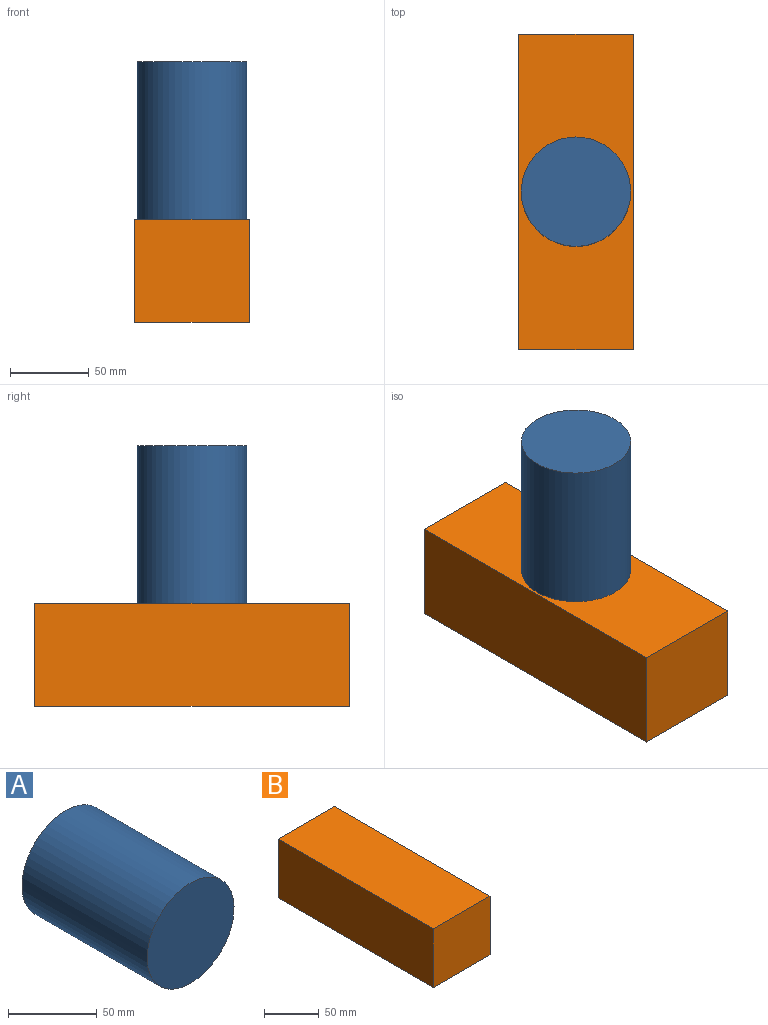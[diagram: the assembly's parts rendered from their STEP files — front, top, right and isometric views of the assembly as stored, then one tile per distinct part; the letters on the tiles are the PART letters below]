
ASSEMBLY  parts=2 mates=1
PART A: 3 faces, bbox 69.4x100x69.4 mm
  f0: cylinder r=34.71mm len=100mm, axis (0,1,0), area 21808.6mm2, adj f1,f2
  f1: plane 69.42x69.42mm, normal (0,-1,0), area 3784.8mm2, adj f0
  f2: plane 69.42x69.42mm, normal (0,1,0), area 3784.8mm2, adj f0
PART B: 6 faces, bbox 72.8x200x65.5 mm
  f0: plane 200x72.78mm, normal (0,0,1), area 14555.2mm2, adj f1,f3,f4,f5
  f1: plane 200x65.5mm, normal (-1,0,0), area 13099.7mm2, adj f0,f2,f4,f5
  f2: plane 200x72.78mm, normal (0,0,-1), area 14555.2mm2, adj f1,f3,f4,f5
  f3: plane 200x65.5mm, normal (1,0,0), area 13099.7mm2, adj f0,f2,f4,f5
  f4: plane 72.78x65.5mm, normal (0,-1,0), area 4766.7mm2, adj f0,f1,f2,f3
  f5: plane 72.78x65.5mm, normal (0,1,0), area 4766.7mm2, adj f0,f1,f2,f3
PLACE A rot(axis=(1,0,0),90deg) t=(-56.25,-17.72,154.89)mm
PLACE B t=(-66.65,82.28,23.35)mm
MATE planar A.f0 <-> B.f0  axis (0,0,-1) through (-56.25,-17.72,54.89)mm
